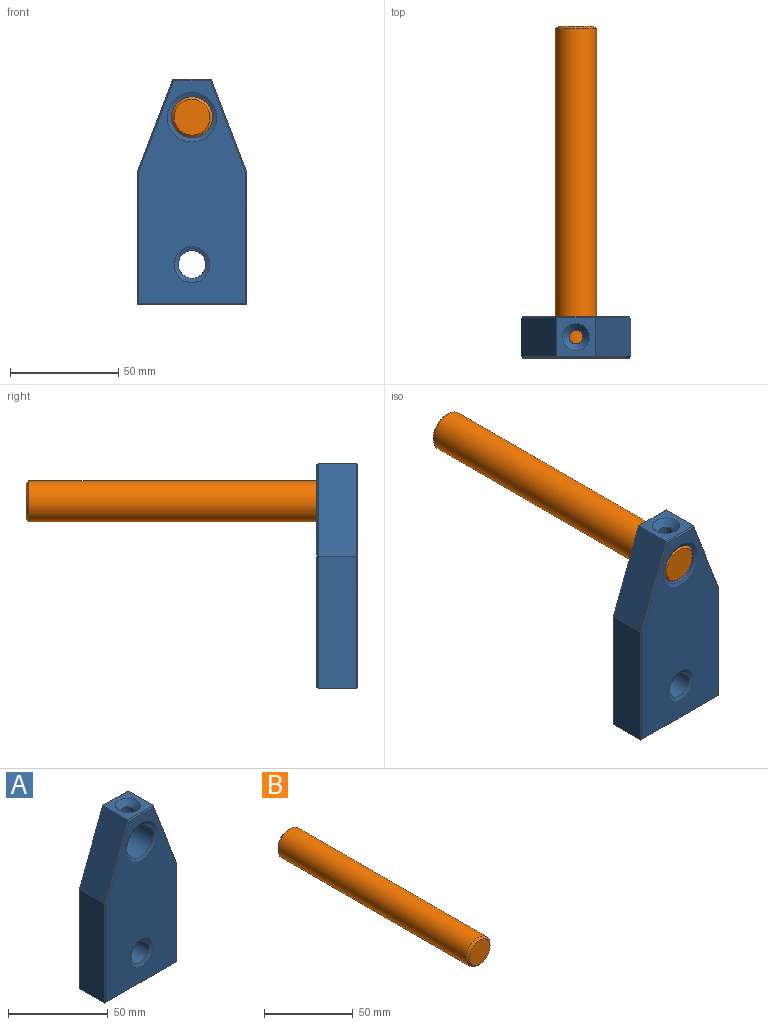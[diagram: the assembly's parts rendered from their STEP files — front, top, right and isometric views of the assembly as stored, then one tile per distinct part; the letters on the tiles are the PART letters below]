
ASSEMBLY  parts=2 mates=1
PART A: 28 faces, bbox 50.8x19x104.1 mm
  f0: plane 17.78x17.73mm, normal (0,0,1), area 192.9mm2, adj f1,f7,f15,f21,f23
  f1: plane 43.18x17.73mm, normal (-0.93,0,0.36), area 819.6mm2, adj f0,f2,f16,f22
  f2: plane 60.96x17.73mm, normal (-1,0,0), area 1080.8mm2, adj f1,f3,f14,f20
  f3: plane 50.8x17.73mm, normal (0,0,-1), area 900.6mm2, adj f2,f4,f12,f18
  f4: plane 60.96x17.73mm, normal (1,0,0), area 1080.8mm2, adj f3,f7,f11,f17
  f5: cylinder r=9.53mm len=19.05mm, axis (0,1,0), area 1010.5mm2, adj f10,f25,f26
  f6: cylinder r=6.35mm len=17.42mm, axis (0,1,0), area 695.1mm2, adj f24,f27
  f7: plane 43.18x17.73mm, normal (0.93,0,0.36), area 819.6mm2, adj f0,f4,f13,f19
  f8: plane 102.87x49.53mm, normal (0,-1,0), area 3774.7mm2, adj f17,f18,f19,f20,f21,f22,f26,f27
  f9: plane 102.87x49.53mm, normal (0,1,0), area 3774.7mm2, adj f11,f12,f13,f14,f15,f16,f24,f25
  f10: cylinder r=3.17mm len=6.35mm, axis (0,0,1), area 104.3mm2, adj f5,f23
  f11: plane 60.96x0.64mm, normal (0.71,0.71,0), area 54.4mm2, adj f4,f9,f12,f13
  f12: plane 50.8x0.64mm, normal (0,0.71,-0.71), area 45mm2, adj f3,f9,f11,f14
  f13: plane 43.3x16.95mm, normal (0.66,0.71,0.25), area 41.3mm2, adj f7,f9,f11,f15
  f14: plane 60.96x0.64mm, normal (-0.71,0.71,0), area 54.4mm2, adj f2,f9,f12,f16
  f15: plane 17.78x0.64mm, normal (0,0.71,0.71), area 15.6mm2, adj f0,f9,f13,f16
  f16: plane 43.3x16.95mm, normal (-0.66,0.71,0.25), area 41.3mm2, adj f1,f9,f14,f15
  f17: plane 60.96x0.64mm, normal (0.71,-0.71,0), area 54.4mm2, adj f4,f8,f18,f19
  f18: plane 50.8x0.64mm, normal (0,-0.71,-0.71), area 45mm2, adj f3,f8,f17,f20
  f19: plane 43.3x16.95mm, normal (0.66,-0.71,0.25), area 41.3mm2, adj f7,f8,f17,f21
  f20: plane 60.96x0.64mm, normal (-0.71,-0.71,0), area 54.4mm2, adj f2,f8,f18,f22
  f21: plane 17.78x0.64mm, normal (0,-0.71,0.71), area 15.6mm2, adj f0,f8,f19,f22
  f22: plane 43.3x16.95mm, normal (-0.66,-0.71,0.25), area 41.3mm2, adj f1,f8,f20,f21
  f23: cone r=3.17mm half-angle=45deg, axis (0,0,1), area 128.3mm2, adj f0,f10
  f24: cone r=8.26mm half-angle=67.5deg, axis (0,1,0), area 94.6mm2, adj f6,f9
  f25: cone r=11.43mm half-angle=67.5deg, axis (0,1,0), area 135.7mm2, adj f5,f9
  f26: cone r=11.43mm half-angle=67.5deg, axis (0,-1,0), area 135.7mm2, adj f5,f8
  f27: cone r=8.26mm half-angle=67.5deg, axis (0,-1,0), area 94.6mm2, adj f6,f8
PART B: 5 faces, bbox 19.1x152.4x19.1 mm
  f0: cylinder r=9.53mm len=149.86mm, axis (0,1,0), area 8968.7mm2, adj f3,f4
  f1: plane 16.51x16.51mm, normal (0,-1,0), area 214.1mm2, adj f4
  f2: plane 16.51x16.51mm, normal (0,1,0), area 214.1mm2, adj f3
  f3: cone r=9.53mm half-angle=45deg, axis (0,-1,0), area 100.3mm2, adj f0,f2
  f4: cone r=8.26mm half-angle=45deg, axis (0,1,0), area 100.3mm2, adj f0,f1
PLACE A t=(107.77,-89.51,-55.46)mm
PLACE B t=(-41.35,44.68,-11.46)mm
MATE slider A.f5 <-> B.f0  axis (0,1,0) through (-41.35,-107.72,-11.46)mm
